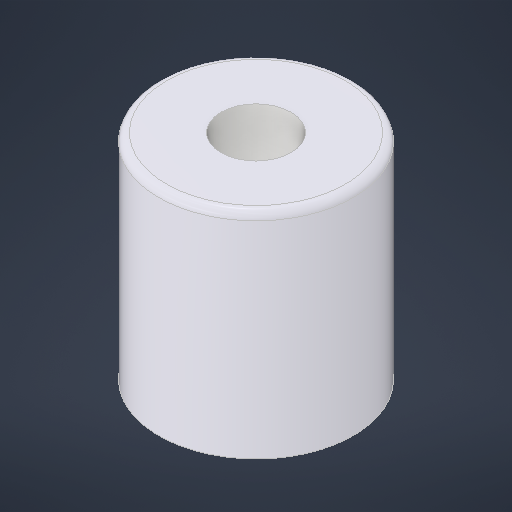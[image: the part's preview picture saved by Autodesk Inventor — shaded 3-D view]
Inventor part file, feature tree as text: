
AUTODESK INVENTOR PART (.ipt)
format: ipt  version: 2025.3 (Build 293356000, 356)  size: 205,824 bytes
history: native  units: in
note: dims shown in document units (in); Inventor stores cm internally (conversion verified against a paired STEP export)
features: extrude x2, fillet x1
ambient origin geometry x8: Origin, YZ Plane, XZ Plane, XY Plane, X Axis, Y Axis, Z Axis, Center Point
bodies: Solid1 (feature_tree)
feature tree (3):
  extrude  "Extrusion1"  Depth=0.1969in
  fillet  "Fillet1"  Radius=0.2165in
  extrude  "Extrusion2"  Depth=0.0079in
